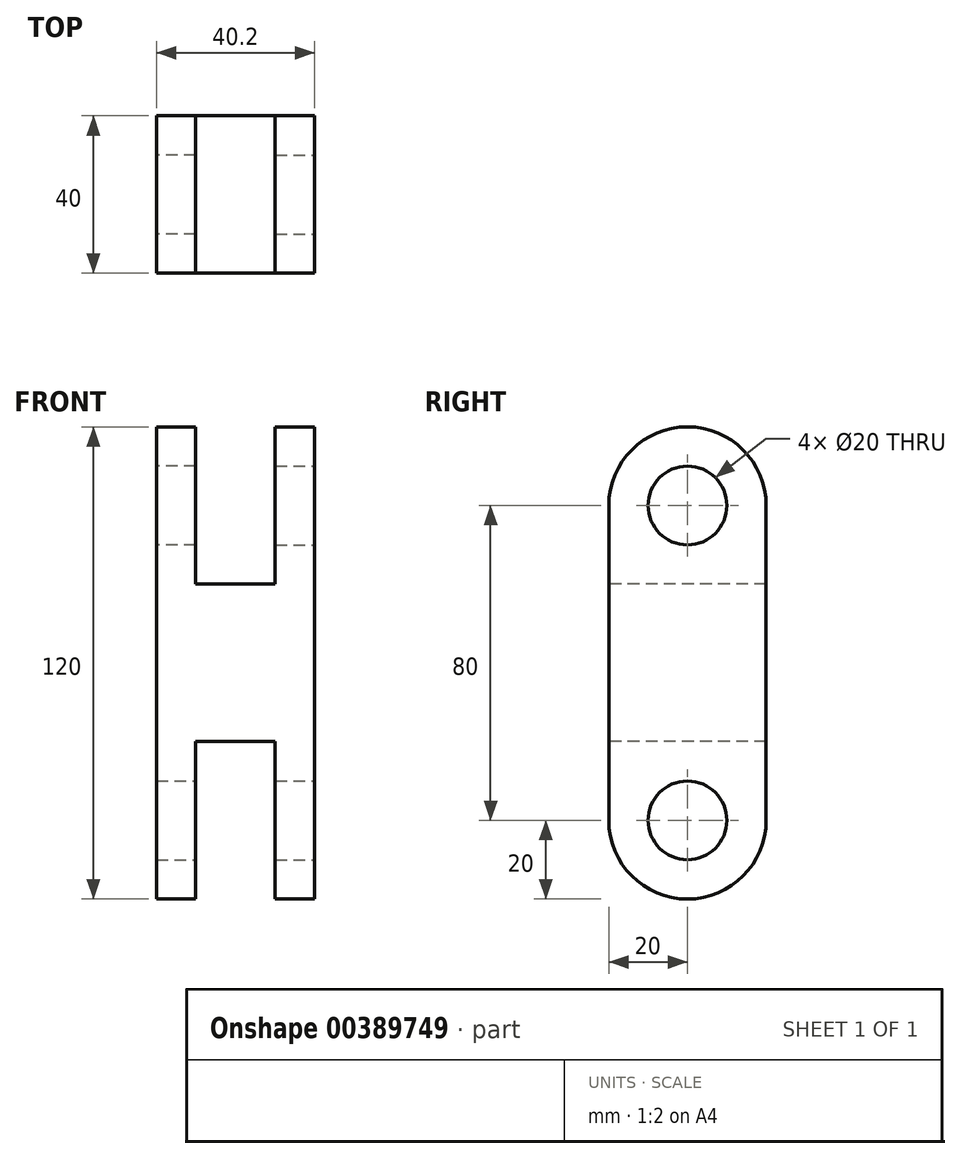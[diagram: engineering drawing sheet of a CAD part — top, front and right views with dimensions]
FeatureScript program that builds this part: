
annotation { "Feature Type Name" : "Feature", "Feature Type Description" : "" }
export const myFeature = defineFeature(function(context is Context, id is Id, definition is map)
    precondition{}
    {
        {
            var Q0;
            Q0=qCreatedBy(makeId("Right.planeOp"),FACE);
            var sketch = newSketch(context, id + "F0", { "sketchPlane" : qUnion([Q0])});
            skLineSegment(sketch, "E0.bottom", {"start": v(20, -40) * mm, "end": v(-20, -40) * mm});
            skLineSegment(sketch, "E0.top", {"start": v(20, 40) * mm, "end": v(-20, 40) * mm});
            skLineSegment(sketch, "E0.left", {"start": v(20, -40) * mm, "end": v(20, 40) * mm});
            skLineSegment(sketch, "E0.right", {"start": v(-20, -40) * mm, "end": v(-20, 40) * mm});
            skPoint(sketch, "E0.middle", {"position": v(0, 0) * mm});
            skSolve(sketch);
        }
        {
            var Q0;
            Q0 = qSketchRegion(id + "F0", true);
            extrude(context, id + "F1", {"entities" : qUnion([Q0]), "depth" : 20.1 * mm});
        }
        {
            var Q0;
            Q0=makeQuery(id+"F1.opExtrude","CAP_FACE",FACE,{"disambiguationData":[OSD([sQuery(id+"F0.wireOp",EDGE,"E0.bottom"),sQuery(id+"F0.wireOp",EDGE,"E0.top"),sQuery(id+"F0.wireOp",EDGE,"E0.left"),sQuery(id+"F0.wireOp",EDGE,"E0.right")])],"isStart":false});
            var sketch = newSketch(context, id + "F2", { "sketchPlane" : qUnion([Q0])});
            skLineSegment(sketch, "E1.bottom", {"start": v(-20, 40) * mm, "end": v(20, 40) * mm});
            skLineSegment(sketch, "E1.left", {"start": v(-20, 40) * mm, "end": v(-20, 60) * mm});
            skLineSegment(sketch, "E1.right", {"start": v(20, 40) * mm, "end": v(20, 60) * mm});
            skArc(sketch, "E2", {"start": v(20, 60) * mm, "mid": v(0, 80) * mm, "end": v(-20, 60) * mm});
            skCircle(sketch, "E3", {"center": v(0, 60) * mm, "radius": 10 * mm});
            skSolve(sketch);
        }
        {
            var Q0;
            Q0 = qSketchRegion(id + "F2", true);
            extrude(context, id + "F3", {"entities" : qUnion([Q0]), "operationType" : NewBodyOperationType.ADD, "oppositeDirection" : true, "depth" : 10 * mm});
        }
        {
            var Q0;
            Q0=makeQuery(id+"F1.opExtrude","SWEPT_BODY",BODY,{"disambiguationData":[OSD([sQuery(id+"F0.wireOp",EDGE,"E0.bottom"),sQuery(id+"F0.wireOp",EDGE,"E0.top"),sQuery(id+"F0.wireOp",EDGE,"E0.left"),sQuery(id+"F0.wireOp",EDGE,"E0.right")])]});
            var Q1;
            Q1=makeQuery(id+"F1.opExtrude","CAP_FACE",FACE,{"disambiguationData":[OSD([sQuery(id+"F0.wireOp",EDGE,"E0.bottom"),sQuery(id+"F0.wireOp",EDGE,"E0.top"),sQuery(id+"F0.wireOp",EDGE,"E0.left"),sQuery(id+"F0.wireOp",EDGE,"E0.right")])],"isStart":true});
            mirror(context, id + "F4", {"operationType" : NewBodyOperationType.ADD, "entities" : qUnion([Q0]), "mirrorPlane" : qUnion([Q1])});
        }
        {
            var Q0;
            {var subQ0=makeQuery(id+"F3.boolean.opBoolean","MERGE",FACE,{"derivedFrom":[makeQuery(id+"F1.opExtrude","SWEPT_FACE",FACE,{"disambiguationData":[OSD([sQuery(id+"F0.wireOp",EDGE,"E0.right")])]}),makeQuery(id+"F3.opExtrude","SWEPT_FACE",FACE,{"disambiguationData":[OSD([sQuery(id+"F2.wireOp",EDGE,"E1.left")])]})]});Q0=makeQuery(id+"F4.boolean.opBoolean","MERGE",FACE,{"derivedFrom":[subQ0,makeQuery(id+"F4.opPattern","COPY",FACE,{"derivedFrom":subQ0,"instanceName":"1"})]});}
            var sketch = newSketch(context, id + "F5", { "sketchPlane" : qUnion([Q0])});
            skPoint(sketch, "E4.middle", {"position": v(0, -40) * mm});
            skLineSegment(sketch, "E5.bottom", {"start": v(-10.1, -40) * mm, "end": v(10.1, -40) * mm});
            skLineSegment(sketch, "E5.top", {"start": v(-10.1, 0) * mm, "end": v(10.1, 0) * mm});
            skLineSegment(sketch, "E5.left", {"start": v(-10.1, -40) * mm, "end": v(-10.1, 0) * mm});
            skLineSegment(sketch, "E5.right", {"start": v(10.1, -40) * mm, "end": v(10.1, 0) * mm});
            skSolve(sketch);
        }
        {
            var Q0;
            Q0 = qSketchRegion(id + "F5", true);
            var Q1;
            {var subQ0=makeQuery(id+"F3.boolean.opBoolean","MERGE",FACE,{"derivedFrom":[makeQuery(id+"F1.opExtrude","SWEPT_FACE",FACE,{"disambiguationData":[OSD([sQuery(id+"F0.wireOp",EDGE,"E0.left")])]}),makeQuery(id+"F3.opExtrude","SWEPT_FACE",FACE,{"disambiguationData":[OSD([sQuery(id+"F2.wireOp",EDGE,"E1.right")])]})]});Q1=makeQuery(id+"F4.boolean.opBoolean","MERGE",FACE,{"derivedFrom":[subQ0,makeQuery(id+"F4.opPattern","COPY",FACE,{"derivedFrom":subQ0,"instanceName":"1"})]});}
            extrude(context, id + "F6", {"entities" : qUnion([Q0]), "operationType" : NewBodyOperationType.REMOVE, "endBound" : BoundingType.UP_TO_SURFACE, "oppositeDirection" : true, "endBoundEntityFace" : qUnion([Q1]), "depth" : 40.2 * mm});
        }
        {
            var Q0;
            Q0=makeQuery(id+"F3.boolean.opBoolean","MERGE",FACE,{"derivedFrom":[makeQuery(id+"F1.opExtrude","CAP_FACE",FACE,{"disambiguationData":[OSD([sQuery(id+"F0.wireOp",EDGE,"E0.bottom"),sQuery(id+"F0.wireOp",EDGE,"E0.top"),sQuery(id+"F0.wireOp",EDGE,"E0.left"),sQuery(id+"F0.wireOp",EDGE,"E0.right")])],"isStart":false}),makeQuery(id+"F3.opExtrude","CAP_FACE",FACE,{"disambiguationData":[OSD([sQuery(id+"F2.wireOp",EDGE,"E1.bottom"),sQuery(id+"F2.wireOp",EDGE,"E1.left"),sQuery(id+"F2.wireOp",EDGE,"E1.right"),sQuery(id+"F2.wireOp",EDGE,"E2"),sQuery(id+"F2.wireOp",EDGE,"E3")])],"isStart":true})]});
            var sketch = newSketch(context, id + "F7", { "sketchPlane" : qUnion([Q0])});
            skPoint(sketch, "E6.endSnap0", {"position": v(0, -40) * mm});
            skLineSegment(sketch, "E7", {"start": v(0, -40) * mm, "end": v(0, -20) * mm, "construction": true});
            skCircle(sketch, "E8", {"center": v(0, -20) * mm, "radius": 10 * mm});
            skSolve(sketch);
        }
        {
            var Q0;
            Q0 = qSketchRegion(id + "F7", true);
            var Q1;
            Q1=makeQuery(id+"F4.opPattern","COPY",FACE,{"derivedFrom":makeQuery(id+"F3.boolean.opBoolean","MERGE",FACE,{"derivedFrom":[makeQuery(id+"F1.opExtrude","CAP_FACE",FACE,{"disambiguationData":[OSD([sQuery(id+"F0.wireOp",EDGE,"E0.bottom"),sQuery(id+"F0.wireOp",EDGE,"E0.top"),sQuery(id+"F0.wireOp",EDGE,"E0.left"),sQuery(id+"F0.wireOp",EDGE,"E0.right")])],"isStart":false}),makeQuery(id+"F3.opExtrude","CAP_FACE",FACE,{"disambiguationData":[OSD([sQuery(id+"F2.wireOp",EDGE,"E1.bottom"),sQuery(id+"F2.wireOp",EDGE,"E1.left"),sQuery(id+"F2.wireOp",EDGE,"E1.right"),sQuery(id+"F2.wireOp",EDGE,"E2"),sQuery(id+"F2.wireOp",EDGE,"E3")])],"isStart":true})]}),"instanceName":"1"});
            extrude(context, id + "F8", {"entities" : qUnion([Q0]), "operationType" : NewBodyOperationType.REMOVE, "endBound" : BoundingType.UP_TO_SURFACE, "oppositeDirection" : true, "endBoundEntityFace" : qUnion([Q1]), "depth" : 40.2 * mm});
        }
        {
            var Q0;
            {var subQ2=sQuery(id+"F0.wireOp",EDGE,"E0.left");var subQ4=sQuery(id+"F0.wireOp",EDGE,"E0.bottom");var subQ6=makeQuery(id+"F1.opExtrude","SWEPT_EDGE",EDGE,{"disambiguationData":[OSD([subQ4,subQ2])]});Q0=makeQuery(id+"F6.boolean.opBoolean","SPLIT",EDGE,{"disambiguationData":[TD([makeQuery(id+"F6.opExtrude","SWEPT_FACE",FACE,{"disambiguationData":[OSD([sQuery(id+"F5.wireOp",EDGE,"E5.left")])]})])],"derivedFrom":makeQuery(id+"F4.boolean.opBoolean","MERGE",EDGE,{"derivedFrom":[subQ6,makeQuery(id+"F4.opPattern","COPY",EDGE,{"derivedFrom":subQ6,"instanceName":"1"})]})});}
            var Q1;
            {var subQ2=sQuery(id+"F0.wireOp",EDGE,"E0.bottom");var subQ4=sQuery(id+"F0.wireOp",EDGE,"E0.right");var subQ6=makeQuery(id+"F1.opExtrude","SWEPT_EDGE",EDGE,{"disambiguationData":[OSD([subQ2,subQ4])]});Q1=makeQuery(id+"F6.boolean.opBoolean","SPLIT",EDGE,{"disambiguationData":[TD([makeQuery(id+"F6.opExtrude","SWEPT_FACE",FACE,{"disambiguationData":[OSD([sQuery(id+"F5.wireOp",EDGE,"E5.left")])]})])],"derivedFrom":makeQuery(id+"F4.boolean.opBoolean","MERGE",EDGE,{"derivedFrom":[subQ6,makeQuery(id+"F4.opPattern","COPY",EDGE,{"derivedFrom":subQ6,"instanceName":"1"})]})});}
            var Q2;
            {var subQ1=sQuery(id+"F0.wireOp",EDGE,"E0.left");var subQ2=sQuery(id+"F0.wireOp",EDGE,"E0.bottom");var subQ6=makeQuery(id+"F1.opExtrude","SWEPT_EDGE",EDGE,{"disambiguationData":[OSD([subQ2,subQ1])]});Q2=makeQuery(id+"F6.boolean.opBoolean","SPLIT",EDGE,{"disambiguationData":[TD([makeQuery(id+"F6.opExtrude","SWEPT_FACE",FACE,{"disambiguationData":[OSD([sQuery(id+"F5.wireOp",EDGE,"E5.right")])]})])],"derivedFrom":makeQuery(id+"F4.boolean.opBoolean","MERGE",EDGE,{"derivedFrom":[subQ6,makeQuery(id+"F4.opPattern","COPY",EDGE,{"derivedFrom":subQ6,"instanceName":"1"})]})});}
            var Q3;
            {var subQ1=sQuery(id+"F0.wireOp",EDGE,"E0.right");var subQ2=sQuery(id+"F0.wireOp",EDGE,"E0.bottom");var subQ6=makeQuery(id+"F1.opExtrude","SWEPT_EDGE",EDGE,{"disambiguationData":[OSD([subQ2,subQ1])]});Q3=makeQuery(id+"F6.boolean.opBoolean","SPLIT",EDGE,{"disambiguationData":[TD([makeQuery(id+"F6.opExtrude","SWEPT_FACE",FACE,{"disambiguationData":[OSD([sQuery(id+"F5.wireOp",EDGE,"E5.right")])]})])],"derivedFrom":makeQuery(id+"F4.boolean.opBoolean","MERGE",EDGE,{"derivedFrom":[subQ6,makeQuery(id+"F4.opPattern","COPY",EDGE,{"derivedFrom":subQ6,"instanceName":"1"})]})});}
            fillet(context, id + "F9", {"entities" : qUnion([Q0, Q1, Q2, Q3]), "radius" : 20 * mm, "tangentPropagation" : true, "allowEdgeOverflow" : false});
        }
    });
